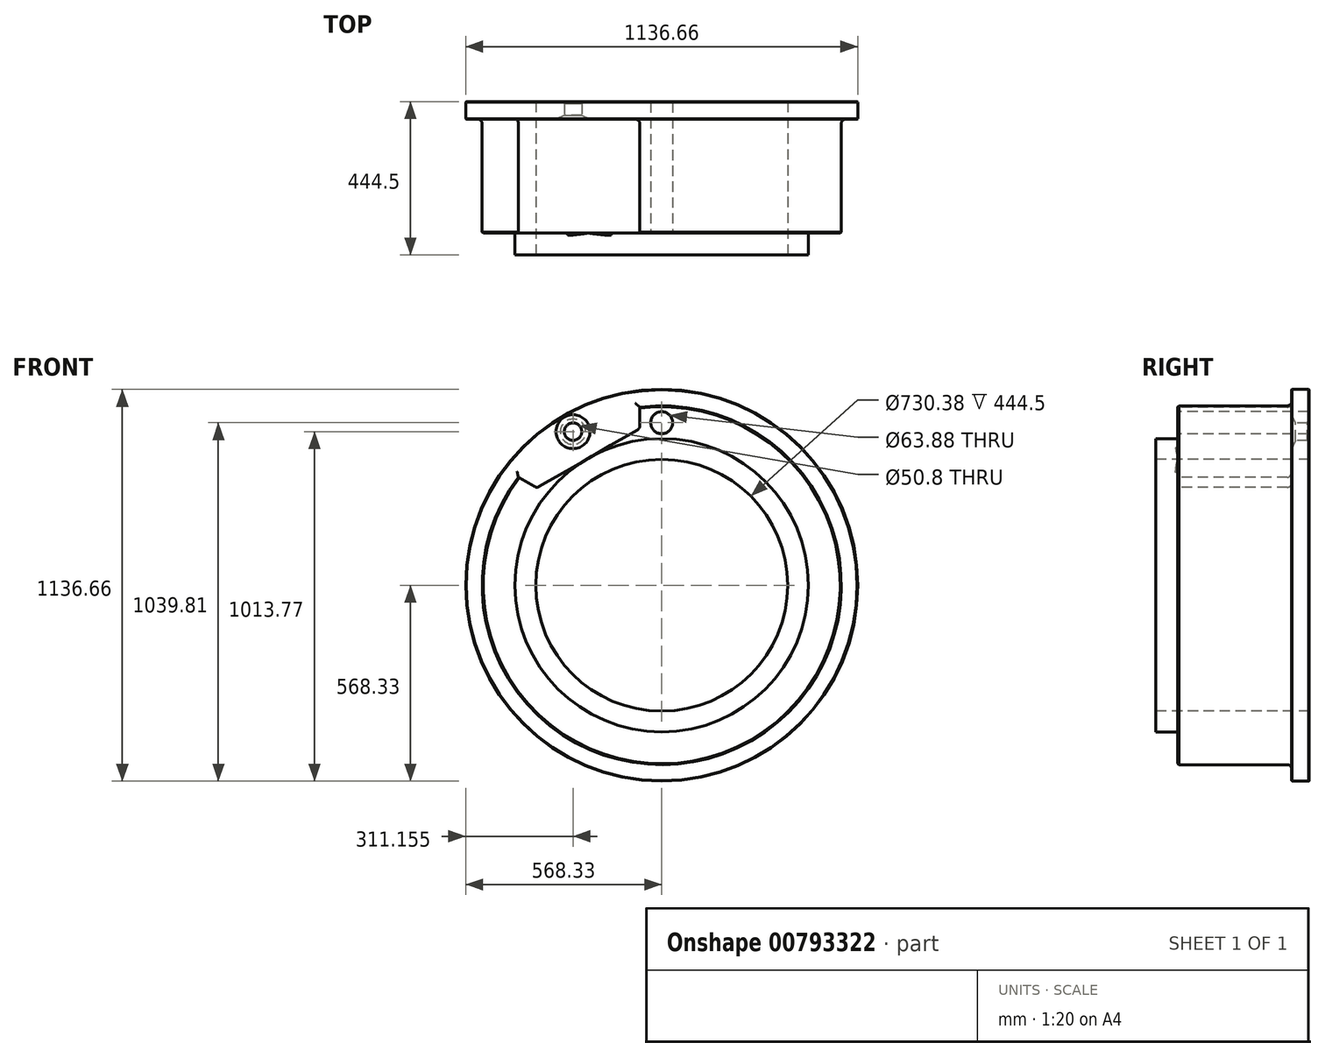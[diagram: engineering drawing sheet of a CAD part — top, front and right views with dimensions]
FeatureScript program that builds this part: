
annotation { "Feature Type Name" : "Feature", "Feature Type Description" : "" }
export const myFeature = defineFeature(function(context is Context, id is Id, definition is map)
    precondition{}
    {
        {
            var Q0;
            Q0=qCreatedBy(makeId("Front.planeOp"),FACE);
            var sketch = newSketch(context, id + "F0", { "sketchPlane" : qUnion([Q0])});
            skCircle(sketch, "E0", {"center": v(0, 0) * mm, "radius": 568.33 * mm});
            skSolve(sketch);
        }
        {
            var Q0;
            Q0 = qSketchRegion(id + "F0", true);
            extrude(context, id + "F1", {"entities" : qUnion([Q0]), "oppositeDirection" : true, "depth" : 444.5 * mm, "offsetDistance" : 25.4 * mm});
        }
        {
            var Q0;
            Q0=qCreatedBy(makeId("Front.planeOp"),FACE);
            var sketch = newSketch(context, id + "F2", { "sketchPlane" : qUnion([Q0])});
            skCircle(sketch, "E1", {"center": v(0, 0) * mm, "radius": 520.7 * mm});
            skCircle(sketch, "E2", {"center": v(0, 0) * mm, "radius": 587 * mm});
            skSolve(sketch);
        }
        {
            var Q0;
            Q0 = qSketchRegion(id + "F2", true);
            extrude(context, id + "F3", {"entities" : qUnion([Q0]), "operationType" : NewBodyOperationType.REMOVE, "oppositeDirection" : true, "depth" : 393.7 * mm, "offsetDistance" : 25.4 * mm});
        }
        {
            var Q0;
            Q0=qCreatedBy(makeId("Front.planeOp"),FACE);
            var sketch = newSketch(context, id + "F4", { "sketchPlane" : qUnion([Q0])});
            skCircle(sketch, "E3", {"center": v(0, 0) * mm, "radius": 425.45 * mm});
            skCircle(sketch, "E4", {"center": v(0, 0) * mm, "radius": 543.88 * mm});
            skSolve(sketch);
        }
        {
            var Q0;
            Q0 = qSketchRegion(id + "F4", true);
            extrude(context, id + "F5", {"entities" : qUnion([Q0]), "operationType" : NewBodyOperationType.REMOVE, "oppositeDirection" : true, "depth" : 63.5 * mm, "offsetDistance" : 25.4 * mm});
        }
        {
            var Q0;
            Q0=qCreatedBy(makeId("Front.planeOp"),FACE);
            var sketch = newSketch(context, id + "F6", { "sketchPlane" : qUnion([Q0])});
            skLineSegment(sketch, "E5", {"start": v(-63.5, 533.78) * mm, "end": v(-63.5, 454.6) * mm});
            skLineSegment(sketch, "E6", {"start": v(-430.52, 321.88) * mm, "end": v(-361.95, 282.3) * mm});
            skLineSegment(sketch, "E7", {"start": v(-63.5, 454.6) * mm, "end": v(-361.95, 282.3) * mm});
            skArc(sketch, "E8", {"start": v(-63.5, 533.78) * mm, "mid": v(-268.77, 465.53) * mm, "end": v(-430.52, 321.88) * mm});
            skSolve(sketch);
        }
        {
            var Q0;
            Q0 = qSketchRegion(id + "F6", true);
            extrude(context, id + "F7", {"entities" : qUnion([Q0]), "operationType" : NewBodyOperationType.REMOVE, "oppositeDirection" : true, "depth" : 393.7 * mm, "offsetDistance" : 25.4 * mm});
        }
        {
            var Q0;
            Q0=qCreatedBy(makeId("Front.planeOp"),FACE);
            var sketch = newSketch(context, id + "F8", { "sketchPlane" : qUnion([Q0])});
            skCircle(sketch, "E9", {"center": v(0, 0) * mm, "radius": 365.19 * mm});
            skSolve(sketch);
        }
        {
            var Q0;
            Q0 = qSketchRegion(id + "F8", true);
            extrude(context, id + "F9", {"entities" : qUnion([Q0]), "operationType" : NewBodyOperationType.REMOVE, "oppositeDirection" : true, "depth" : 447.04 * mm, "offsetDistance" : 25.4 * mm});
        }
        {
            var Q0;
            {var subQ0=sQuery(id+"F4.wireOp",EDGE,"E3");var subQ2=makeQuery(id+"F5.boolean.opBoolean","COPY",FACE,{"derivedFrom":makeQuery(id+"F5.opExtrude","CAP_FACE",FACE,{"disambiguationData":[OSD([subQ0,sQuery(id+"F4.wireOp",EDGE,"E4")])],"isStart":false})});Q0=makeQuery(id+"FbK9JrwXL36KEKy_1.1.F7.boolean.opBoolean","SPLIT",FACE,{"disambiguationData":[TD([makeQuery(id+"F7.boolean.opBoolean","COPY",FACE,{"derivedFrom":makeQuery(id+"F7.opExtrude","SWEPT_FACE",FACE,{"disambiguationData":[OSD([sQuery(id+"F6.wireOp",EDGE,"E6")])]})})])],"derivedFrom":subQ2});}
            var sketch = newSketch(context, id + "F10", { "sketchPlane" : qUnion([Q0])});
            skCircle(sketch, "E10", {"center": v(0, 471.47) * mm, "radius": 31.94 * mm});
            skSolve(sketch);
        }
        {
            var Q0;
            Q0 = qSketchRegion(id + "F10", true);
            extrude(context, id + "F11", {"entities" : qUnion([Q0]), "operationType" : NewBodyOperationType.REMOVE, "oppositeDirection" : true, "depth" : 447.04 * mm, "offsetDistance" : 25.4 * mm});
        }
        {
            var Q0;
            Q0=makeQuery(id+"F11.boolean.opBoolean","COPY",EDGE,{"derivedFrom":makeQuery(id+"F11.opExtrude","CAP_EDGE",EDGE,{"disambiguationData":[OSD([sQuery(id+"F10.wireOp",EDGE,"E10")])],"isStart":true})});
            var Q1;
            Q1=makeQuery(id+"FKzMlxL366D46Dd_1.1.F11.boolean.opBoolean","COPY",EDGE,{"derivedFrom":makeQuery(id+"FKzMlxL366D46Dd_1.1.F11.opExtrude","CAP_EDGE",EDGE,{"disambiguationData":[OSD([sQuery(id+"F10.wireOp",EDGE,"E10")])],"isStart":true})});
            var Q2;
            Q2=makeQuery(id+"FKzMlxL366D46Dd_1.2.F11.boolean.opBoolean","COPY",EDGE,{"derivedFrom":makeQuery(id+"FKzMlxL366D46Dd_1.2.F11.opExtrude","CAP_EDGE",EDGE,{"disambiguationData":[OSD([sQuery(id+"F10.wireOp",EDGE,"E10")])],"isStart":true})});
            var Q3;
            Q3=makeQuery(id+"FKzMlxL366D46Dd_1.3.F11.boolean.opBoolean","COPY",EDGE,{"derivedFrom":makeQuery(id+"FKzMlxL366D46Dd_1.3.F11.opExtrude","CAP_EDGE",EDGE,{"disambiguationData":[OSD([sQuery(id+"F10.wireOp",EDGE,"E10")])],"isStart":true})});
            var Q4;
            Q4=makeQuery(id+"FKzMlxL366D46Dd_1.4.F11.boolean.opBoolean","COPY",EDGE,{"derivedFrom":makeQuery(id+"FKzMlxL366D46Dd_1.4.F11.opExtrude","CAP_EDGE",EDGE,{"disambiguationData":[OSD([sQuery(id+"F10.wireOp",EDGE,"E10")])],"isStart":true})});
            var Q5;
            Q5=makeQuery(id+"FKzMlxL366D46Dd_1.5.F11.boolean.opBoolean","COPY",EDGE,{"derivedFrom":makeQuery(id+"FKzMlxL366D46Dd_1.5.F11.opExtrude","CAP_EDGE",EDGE,{"disambiguationData":[OSD([sQuery(id+"F10.wireOp",EDGE,"E10")])],"isStart":true})});
            var Q6;
            Q6=makeQuery(id+"FKzMlxL366D46Dd_1.5.F11.boolean.opBoolean","INTERSECT",EDGE,{"derivedFrom":[makeQuery(id+"F1.opExtrude","CAP_FACE",FACE,{"disambiguationData":[OSD([sQuery(id+"F0.wireOp",EDGE,"E0")])],"isStart":false}),makeQuery(id+"FKzMlxL366D46Dd_1.5.F11.opExtrude","SWEPT_FACE",FACE,{"disambiguationData":[OSD([sQuery(id+"F10.wireOp",EDGE,"E10")])]})]});
            var Q7;
            Q7=makeQuery(id+"FKzMlxL366D46Dd_1.4.F11.boolean.opBoolean","INTERSECT",EDGE,{"derivedFrom":[makeQuery(id+"F1.opExtrude","CAP_FACE",FACE,{"disambiguationData":[OSD([sQuery(id+"F0.wireOp",EDGE,"E0")])],"isStart":false}),makeQuery(id+"FKzMlxL366D46Dd_1.4.F11.opExtrude","SWEPT_FACE",FACE,{"disambiguationData":[OSD([sQuery(id+"F10.wireOp",EDGE,"E10")])]})]});
            var Q8;
            Q8=makeQuery(id+"F11.boolean.opBoolean","INTERSECT",EDGE,{"derivedFrom":[makeQuery(id+"F1.opExtrude","CAP_FACE",FACE,{"disambiguationData":[OSD([sQuery(id+"F0.wireOp",EDGE,"E0")])],"isStart":false}),makeQuery(id+"F11.opExtrude","SWEPT_FACE",FACE,{"disambiguationData":[OSD([sQuery(id+"F10.wireOp",EDGE,"E10")])]})]});
            var Q9;
            Q9=makeQuery(id+"FKzMlxL366D46Dd_1.3.F11.boolean.opBoolean","INTERSECT",EDGE,{"derivedFrom":[makeQuery(id+"F1.opExtrude","CAP_FACE",FACE,{"disambiguationData":[OSD([sQuery(id+"F0.wireOp",EDGE,"E0")])],"isStart":false}),makeQuery(id+"FKzMlxL366D46Dd_1.3.F11.opExtrude","SWEPT_FACE",FACE,{"disambiguationData":[OSD([sQuery(id+"F10.wireOp",EDGE,"E10")])]})]});
            var Q10;
            Q10=makeQuery(id+"FKzMlxL366D46Dd_1.1.F11.boolean.opBoolean","INTERSECT",EDGE,{"derivedFrom":[makeQuery(id+"F1.opExtrude","CAP_FACE",FACE,{"disambiguationData":[OSD([sQuery(id+"F0.wireOp",EDGE,"E0")])],"isStart":false}),makeQuery(id+"FKzMlxL366D46Dd_1.1.F11.opExtrude","SWEPT_FACE",FACE,{"disambiguationData":[OSD([sQuery(id+"F10.wireOp",EDGE,"E10")])]})]});
            var Q11;
            Q11=makeQuery(id+"FKzMlxL366D46Dd_1.2.F11.boolean.opBoolean","INTERSECT",EDGE,{"derivedFrom":[makeQuery(id+"F1.opExtrude","CAP_FACE",FACE,{"disambiguationData":[OSD([sQuery(id+"F0.wireOp",EDGE,"E0")])],"isStart":false}),makeQuery(id+"FKzMlxL366D46Dd_1.2.F11.opExtrude","SWEPT_FACE",FACE,{"disambiguationData":[OSD([sQuery(id+"F10.wireOp",EDGE,"E10")])]})]});
            var Q12;
            Q12=makeQuery(id+"F1.opExtrude","CAP_EDGE",EDGE,{"disambiguationData":[OSD([sQuery(id+"F0.wireOp",EDGE,"E0")])],"isStart":false});
            var Q13;
            Q13=makeQuery(id+"F3.boolean.opBoolean","INTERSECT",EDGE,{"derivedFrom":[makeQuery(id+"F1.opExtrude","SWEPT_FACE",FACE,{"disambiguationData":[OSD([sQuery(id+"F0.wireOp",EDGE,"E0")])]}),makeQuery(id+"F3.opExtrude","CAP_FACE",FACE,{"disambiguationData":[OSD([sQuery(id+"F2.wireOp",EDGE,"E1"),sQuery(id+"F2.wireOp",EDGE,"E2")])],"isStart":false})]});
            chamfer(context, id + "F12", {"entities" : qUnion([Q0, Q1, Q2, Q3, Q4, Q5, Q6, Q7, Q8, Q9, Q10, Q11, Q12, Q13]), "width" : 1.52 * mm, "tangentPropagation" : true});
        }
        {
            var Q0;
            {var subQ0=makeQuery(id+"F3.boolean.opBoolean","COPY",FACE,{"derivedFrom":makeQuery(id+"F3.opExtrude","SWEPT_FACE",FACE,{"disambiguationData":[OSD([sQuery(id+"F2.wireOp",EDGE,"E1")])]})});var subQ1=makeQuery(id+"F5.opExtrude","CAP_FACE",FACE,{"disambiguationData":[OSD([sQuery(id+"F4.wireOp",EDGE,"E3"),sQuery(id+"F4.wireOp",EDGE,"E4")])],"isStart":false});Q0=makeQuery(id+"FbK9JrwXL36KEKy_1.1.F7.boolean.opBoolean","SPLIT",EDGE,{"disambiguationData":[TD([makeQuery(id+"F7.boolean.opBoolean","COPY",FACE,{"derivedFrom":makeQuery(id+"F7.opExtrude","SWEPT_FACE",FACE,{"disambiguationData":[OSD([sQuery(id+"F6.wireOp",EDGE,"E6")])]})})])],"derivedFrom":makeQuery(id+"F5.boolean.opBoolean","INTERSECT",EDGE,{"derivedFrom":[subQ0,subQ1]})});}
            var Q1;
            {var subQ0=makeQuery(id+"F3.boolean.opBoolean","COPY",FACE,{"derivedFrom":makeQuery(id+"F3.opExtrude","SWEPT_FACE",FACE,{"disambiguationData":[OSD([sQuery(id+"F2.wireOp",EDGE,"E1")])]})});var subQ1=makeQuery(id+"F5.opExtrude","CAP_FACE",FACE,{"disambiguationData":[OSD([sQuery(id+"F4.wireOp",EDGE,"E3"),sQuery(id+"F4.wireOp",EDGE,"E4")])],"isStart":false});var subQ4=makeQuery(id+"F7.boolean.opBoolean","COPY",FACE,{"derivedFrom":makeQuery(id+"F7.opExtrude","SWEPT_FACE",FACE,{"disambiguationData":[OSD([sQuery(id+"F6.wireOp",EDGE,"E5")])]})});Q1=makeQuery(id+"FbK9JrwXL36KEKy_1.5.F7.boolean.opBoolean","SPLIT",EDGE,{"disambiguationData":[TD([subQ4])],"derivedFrom":makeQuery(id+"FbK9JrwXL36KEKy_1.4.F7.boolean.opBoolean","SPLIT",EDGE,{"disambiguationData":[TD([subQ4])],"derivedFrom":makeQuery(id+"FbK9JrwXL36KEKy_1.3.F7.boolean.opBoolean","SPLIT",EDGE,{"disambiguationData":[TD([subQ4])],"derivedFrom":makeQuery(id+"FbK9JrwXL36KEKy_1.2.F7.boolean.opBoolean","SPLIT",EDGE,{"disambiguationData":[TD([subQ4])],"derivedFrom":makeQuery(id+"FbK9JrwXL36KEKy_1.1.F7.boolean.opBoolean","SPLIT",EDGE,{"disambiguationData":[TD([subQ4])],"derivedFrom":makeQuery(id+"F5.boolean.opBoolean","INTERSECT",EDGE,{"derivedFrom":[subQ0,subQ1]})})})})})});}
            var Q2;
            Q2=makeQuery(id+"F5.boolean.opBoolean","COPY",EDGE,{"derivedFrom":makeQuery(id+"F5.opExtrude","CAP_EDGE",EDGE,{"disambiguationData":[OSD([sQuery(id+"F4.wireOp",EDGE,"E3")])],"isStart":true})});
            var Q3;
            {var subQ0=makeQuery(id+"F3.boolean.opBoolean","COPY",FACE,{"derivedFrom":makeQuery(id+"F3.opExtrude","SWEPT_FACE",FACE,{"disambiguationData":[OSD([sQuery(id+"F2.wireOp",EDGE,"E1")])]})});var subQ1=makeQuery(id+"F5.opExtrude","CAP_FACE",FACE,{"disambiguationData":[OSD([sQuery(id+"F4.wireOp",EDGE,"E3"),sQuery(id+"F4.wireOp",EDGE,"E4")])],"isStart":false});var subQ3=makeQuery(id+"FbK9JrwXL36KEKy_1.1.F7.opExtrude","SWEPT_FACE",FACE,{"disambiguationData":[OSD([sQuery(id+"F6.wireOp",EDGE,"E6")])]});var subQ4=sQuery(id+"F6.wireOp",EDGE,"E5");Q3=makeQuery(id+"FbK9JrwXL36KEKy_1.2.F7.boolean.opBoolean","SPLIT",EDGE,{"disambiguationData":[TD([makeQuery(id+"FbK9JrwXL36KEKy_1.1.F7.boolean.opBoolean","COPY",FACE,{"derivedFrom":subQ3})])],"derivedFrom":makeQuery(id+"FbK9JrwXL36KEKy_1.1.F7.boolean.opBoolean","SPLIT",EDGE,{"disambiguationData":[TD([makeQuery(id+"F7.boolean.opBoolean","COPY",FACE,{"derivedFrom":makeQuery(id+"F7.opExtrude","SWEPT_FACE",FACE,{"disambiguationData":[OSD([subQ4])]})})])],"derivedFrom":makeQuery(id+"F5.boolean.opBoolean","INTERSECT",EDGE,{"derivedFrom":[subQ0,subQ1]})})});}
            var Q4;
            {var subQ0=makeQuery(id+"F3.boolean.opBoolean","COPY",FACE,{"derivedFrom":makeQuery(id+"F3.opExtrude","SWEPT_FACE",FACE,{"disambiguationData":[OSD([sQuery(id+"F2.wireOp",EDGE,"E1")])]})});var subQ1=makeQuery(id+"F5.opExtrude","CAP_FACE",FACE,{"disambiguationData":[OSD([sQuery(id+"F4.wireOp",EDGE,"E3"),sQuery(id+"F4.wireOp",EDGE,"E4")])],"isStart":false});var subQ3=sQuery(id+"F6.wireOp",EDGE,"E5");var subQ4=sQuery(id+"F6.wireOp",EDGE,"E6");var subQ5=makeQuery(id+"FbK9JrwXL36KEKy_1.2.F7.opExtrude","SWEPT_FACE",FACE,{"disambiguationData":[OSD([subQ4])]});var subQ6=makeQuery(id+"F7.boolean.opBoolean","COPY",FACE,{"derivedFrom":makeQuery(id+"F7.opExtrude","SWEPT_FACE",FACE,{"disambiguationData":[OSD([subQ3])]})});Q4=makeQuery(id+"FbK9JrwXL36KEKy_1.3.F7.boolean.opBoolean","SPLIT",EDGE,{"disambiguationData":[TD([makeQuery(id+"FbK9JrwXL36KEKy_1.2.F7.boolean.opBoolean","COPY",FACE,{"derivedFrom":subQ5})])],"derivedFrom":makeQuery(id+"FbK9JrwXL36KEKy_1.2.F7.boolean.opBoolean","SPLIT",EDGE,{"disambiguationData":[TD([subQ6])],"derivedFrom":makeQuery(id+"FbK9JrwXL36KEKy_1.1.F7.boolean.opBoolean","SPLIT",EDGE,{"disambiguationData":[TD([subQ6])],"derivedFrom":makeQuery(id+"F5.boolean.opBoolean","INTERSECT",EDGE,{"derivedFrom":[subQ0,subQ1]})})})});}
            var Q5;
            {var subQ0=makeQuery(id+"F3.boolean.opBoolean","COPY",FACE,{"derivedFrom":makeQuery(id+"F3.opExtrude","SWEPT_FACE",FACE,{"disambiguationData":[OSD([sQuery(id+"F2.wireOp",EDGE,"E1")])]})});var subQ1=makeQuery(id+"F5.opExtrude","CAP_FACE",FACE,{"disambiguationData":[OSD([sQuery(id+"F4.wireOp",EDGE,"E3"),sQuery(id+"F4.wireOp",EDGE,"E4")])],"isStart":false});var subQ3=sQuery(id+"F6.wireOp",EDGE,"E6");var subQ4=makeQuery(id+"FbK9JrwXL36KEKy_1.3.F7.opExtrude","SWEPT_FACE",FACE,{"disambiguationData":[OSD([subQ3])]});var subQ5=sQuery(id+"F6.wireOp",EDGE,"E5");var subQ6=makeQuery(id+"F7.boolean.opBoolean","COPY",FACE,{"derivedFrom":makeQuery(id+"F7.opExtrude","SWEPT_FACE",FACE,{"disambiguationData":[OSD([subQ5])]})});Q5=makeQuery(id+"FbK9JrwXL36KEKy_1.4.F7.boolean.opBoolean","SPLIT",EDGE,{"disambiguationData":[TD([makeQuery(id+"FbK9JrwXL36KEKy_1.3.F7.boolean.opBoolean","COPY",FACE,{"derivedFrom":subQ4})])],"derivedFrom":makeQuery(id+"FbK9JrwXL36KEKy_1.3.F7.boolean.opBoolean","SPLIT",EDGE,{"disambiguationData":[TD([subQ6])],"derivedFrom":makeQuery(id+"FbK9JrwXL36KEKy_1.2.F7.boolean.opBoolean","SPLIT",EDGE,{"disambiguationData":[TD([subQ6])],"derivedFrom":makeQuery(id+"FbK9JrwXL36KEKy_1.1.F7.boolean.opBoolean","SPLIT",EDGE,{"disambiguationData":[TD([subQ6])],"derivedFrom":makeQuery(id+"F5.boolean.opBoolean","INTERSECT",EDGE,{"derivedFrom":[subQ0,subQ1]})})})})});}
            var Q6;
            {var subQ0=makeQuery(id+"F3.boolean.opBoolean","COPY",FACE,{"derivedFrom":makeQuery(id+"F3.opExtrude","SWEPT_FACE",FACE,{"disambiguationData":[OSD([sQuery(id+"F2.wireOp",EDGE,"E1")])]})});var subQ1=makeQuery(id+"F5.opExtrude","CAP_FACE",FACE,{"disambiguationData":[OSD([sQuery(id+"F4.wireOp",EDGE,"E3"),sQuery(id+"F4.wireOp",EDGE,"E4")])],"isStart":false});var subQ3=sQuery(id+"F6.wireOp",EDGE,"E6");var subQ4=makeQuery(id+"FbK9JrwXL36KEKy_1.4.F7.opExtrude","SWEPT_FACE",FACE,{"disambiguationData":[OSD([subQ3])]});var subQ5=sQuery(id+"F6.wireOp",EDGE,"E5");var subQ6=makeQuery(id+"F7.boolean.opBoolean","COPY",FACE,{"derivedFrom":makeQuery(id+"F7.opExtrude","SWEPT_FACE",FACE,{"disambiguationData":[OSD([subQ5])]})});Q6=makeQuery(id+"FbK9JrwXL36KEKy_1.5.F7.boolean.opBoolean","SPLIT",EDGE,{"disambiguationData":[TD([makeQuery(id+"FbK9JrwXL36KEKy_1.4.F7.boolean.opBoolean","COPY",FACE,{"derivedFrom":subQ4})])],"derivedFrom":makeQuery(id+"FbK9JrwXL36KEKy_1.4.F7.boolean.opBoolean","SPLIT",EDGE,{"disambiguationData":[TD([subQ6])],"derivedFrom":makeQuery(id+"FbK9JrwXL36KEKy_1.3.F7.boolean.opBoolean","SPLIT",EDGE,{"disambiguationData":[TD([subQ6])],"derivedFrom":makeQuery(id+"FbK9JrwXL36KEKy_1.2.F7.boolean.opBoolean","SPLIT",EDGE,{"disambiguationData":[TD([subQ6])],"derivedFrom":makeQuery(id+"FbK9JrwXL36KEKy_1.1.F7.boolean.opBoolean","SPLIT",EDGE,{"disambiguationData":[TD([subQ6])],"derivedFrom":makeQuery(id+"F5.boolean.opBoolean","INTERSECT",EDGE,{"derivedFrom":[subQ0,subQ1]})})})})})});}
            chamfer(context, id + "F13", {"entities" : qUnion([Q0, Q1, Q2, Q3, Q4, Q5, Q6]), "width" : 3.05 * mm, "tangentPropagation" : true});
        }
        {
            var Q0;
            {var subQ0=sQuery(id+"F4.wireOp",EDGE,"E3");var subQ2=sQuery(id+"F6.wireOp",EDGE,"E7");var subQ4=makeQuery(id+"FbK9JrwXL36KEKy_1.2.F7.opExtrude","SWEPT_FACE",FACE,{"disambiguationData":[OSD([subQ2])]});Q0=makeQuery(id+"FbK9JrwXL36KEKy_1.3.F7.boolean.opBoolean","SPLIT",EDGE,{"disambiguationData":[TD([makeQuery(id+"FbK9JrwXL36KEKy_1.2.F7.boolean.opBoolean","COPY",FACE,{"derivedFrom":subQ4})])],"derivedFrom":makeQuery(id+"FbK9JrwXL36KEKy_1.2.F7.boolean.opBoolean","SPLIT",EDGE,{"disambiguationData":[TD([makeQuery(id+"F7.boolean.opBoolean","COPY",FACE,{"derivedFrom":makeQuery(id+"F7.opExtrude","SWEPT_FACE",FACE,{"disambiguationData":[OSD([subQ2])]})})])],"derivedFrom":makeQuery(id+"FbK9JrwXL36KEKy_1.1.F7.boolean.opBoolean","SPLIT",EDGE,{"disambiguationData":[OD(0.0)],"derivedFrom":makeQuery(id+"F5.boolean.opBoolean","COPY",EDGE,{"derivedFrom":makeQuery(id+"F5.opExtrude","CAP_EDGE",EDGE,{"disambiguationData":[OSD([subQ0])],"isStart":false})})})})});}
            fillet(context, id + "F14", {"entities" : qUnion([Q0]), "radius" : 6.35 * mm, "tangentPropagation" : true, "allowEdgeOverflow" : false});
        }
        {
            var Q0;
            Q0=makeQuery(id+"FbK9JrwXL36KEKy_1.2.F7.boolean.opBoolean","COPY",EDGE,{"derivedFrom":makeQuery(id+"FbK9JrwXL36KEKy_1.2.F7.opExtrude","SWEPT_EDGE",EDGE,{"disambiguationData":[OSD([sQuery(id+"F6.wireOp",EDGE,"E5"),sQuery(id+"F6.wireOp",EDGE,"E7")])]})});
            var Q1;
            Q1=makeQuery(id+"FbK9JrwXL36KEKy_1.2.F7.boolean.opBoolean","COPY",EDGE,{"derivedFrom":makeQuery(id+"FbK9JrwXL36KEKy_1.2.F7.opExtrude","CAP_EDGE",EDGE,{"disambiguationData":[OSD([sQuery(id+"F6.wireOp",EDGE,"E7")])],"isStart":false})});
            var Q2;
            Q2=makeQuery(id+"FbK9JrwXL36KEKy_1.2.F7.boolean.opBoolean","COPY",EDGE,{"derivedFrom":makeQuery(id+"FbK9JrwXL36KEKy_1.2.F7.opExtrude","SWEPT_EDGE",EDGE,{"disambiguationData":[OSD([sQuery(id+"F6.wireOp",EDGE,"E6"),sQuery(id+"F6.wireOp",EDGE,"E7")])]})});
            var Q3;
            Q3=makeQuery(id+"FbK9JrwXL36KEKy_1.2.F7.boolean.opBoolean","COPY",EDGE,{"derivedFrom":makeQuery(id+"FbK9JrwXL36KEKy_1.2.F7.opExtrude","CAP_EDGE",EDGE,{"disambiguationData":[OSD([sQuery(id+"F6.wireOp",EDGE,"E5")])],"isStart":false})});
            var Q4;
            {var subQ2=sQuery(id+"F6.wireOp",EDGE,"E6");var subQ3=sQuery(id+"F6.wireOp",EDGE,"E5");var subQ5=sQuery(id+"F2.wireOp",EDGE,"E1");var subQ9=makeQuery(id+"FbK9JrwXL36KEKy_1.1.F7.opExtrude","SWEPT_FACE",FACE,{"disambiguationData":[OSD([subQ2])]});Q4=makeQuery(id+"FbK9JrwXL36KEKy_1.2.F7.boolean.opBoolean","SPLIT",EDGE,{"disambiguationData":[TD([makeQuery(id+"FbK9JrwXL36KEKy_1.1.F7.boolean.opBoolean","COPY",FACE,{"derivedFrom":subQ9})])],"derivedFrom":makeQuery(id+"FbK9JrwXL36KEKy_1.1.F7.boolean.opBoolean","SPLIT",EDGE,{"disambiguationData":[TD([makeQuery(id+"F7.boolean.opBoolean","COPY",FACE,{"derivedFrom":makeQuery(id+"F7.opExtrude","SWEPT_FACE",FACE,{"disambiguationData":[OSD([subQ3])]})})])],"derivedFrom":makeQuery(id+"F3.boolean.opBoolean","COPY",EDGE,{"derivedFrom":makeQuery(id+"F3.opExtrude","CAP_EDGE",EDGE,{"disambiguationData":[OSD([subQ5])],"isStart":false})})})});}
            var Q5;
            Q5=makeQuery(id+"FbK9JrwXL36KEKy_1.1.F7.boolean.opBoolean","COPY",EDGE,{"derivedFrom":makeQuery(id+"FbK9JrwXL36KEKy_1.1.F7.opExtrude","CAP_EDGE",EDGE,{"disambiguationData":[OSD([sQuery(id+"F6.wireOp",EDGE,"E7")])],"isStart":false})});
            var Q6;
            Q6=makeQuery(id+"FbK9JrwXL36KEKy_1.1.F7.boolean.opBoolean","COPY",EDGE,{"derivedFrom":makeQuery(id+"FbK9JrwXL36KEKy_1.1.F7.opExtrude","SWEPT_EDGE",EDGE,{"disambiguationData":[OSD([sQuery(id+"F6.wireOp",EDGE,"E5"),sQuery(id+"F6.wireOp",EDGE,"E7")])]})});
            var Q7;
            Q7=makeQuery(id+"FbK9JrwXL36KEKy_1.1.F7.boolean.opBoolean","COPY",EDGE,{"derivedFrom":makeQuery(id+"FbK9JrwXL36KEKy_1.1.F7.opExtrude","CAP_EDGE",EDGE,{"disambiguationData":[OSD([sQuery(id+"F6.wireOp",EDGE,"E5")])],"isStart":false})});
            var Q8;
            {var subQ2=sQuery(id+"F6.wireOp",EDGE,"E6");var subQ4=sQuery(id+"F2.wireOp",EDGE,"E1");Q8=makeQuery(id+"FbK9JrwXL36KEKy_1.1.F7.boolean.opBoolean","SPLIT",EDGE,{"disambiguationData":[TD([makeQuery(id+"F7.boolean.opBoolean","COPY",FACE,{"derivedFrom":makeQuery(id+"F7.opExtrude","SWEPT_FACE",FACE,{"disambiguationData":[OSD([subQ2])]})})])],"derivedFrom":makeQuery(id+"F3.boolean.opBoolean","COPY",EDGE,{"derivedFrom":makeQuery(id+"F3.opExtrude","CAP_EDGE",EDGE,{"disambiguationData":[OSD([subQ4])],"isStart":false})})});}
            var Q9;
            Q9=makeQuery(id+"FbK9JrwXL36KEKy_1.1.F7.boolean.opBoolean","COPY",EDGE,{"derivedFrom":makeQuery(id+"FbK9JrwXL36KEKy_1.1.F7.opExtrude","SWEPT_EDGE",EDGE,{"disambiguationData":[OSD([sQuery(id+"F6.wireOp",EDGE,"E6"),sQuery(id+"F6.wireOp",EDGE,"E7")])]})});
            var Q10;
            Q10=makeQuery(id+"FbK9JrwXL36KEKy_1.1.F7.boolean.opBoolean","COPY",EDGE,{"derivedFrom":makeQuery(id+"FbK9JrwXL36KEKy_1.1.F7.opExtrude","CAP_EDGE",EDGE,{"disambiguationData":[OSD([sQuery(id+"F6.wireOp",EDGE,"E6")])],"isStart":false})});
            var Q11;
            Q11=makeQuery(id+"F7.boolean.opBoolean","COPY",EDGE,{"derivedFrom":makeQuery(id+"F7.opExtrude","CAP_EDGE",EDGE,{"disambiguationData":[OSD([sQuery(id+"F6.wireOp",EDGE,"E6")])],"isStart":false})});
            var Q12;
            Q12=makeQuery(id+"F7.boolean.opBoolean","COPY",EDGE,{"derivedFrom":makeQuery(id+"F7.opExtrude","CAP_EDGE",EDGE,{"disambiguationData":[OSD([sQuery(id+"F6.wireOp",EDGE,"E7")])],"isStart":false})});
            var Q13;
            Q13=makeQuery(id+"F7.boolean.opBoolean","COPY",EDGE,{"derivedFrom":makeQuery(id+"F7.opExtrude","SWEPT_EDGE",EDGE,{"disambiguationData":[OSD([sQuery(id+"F6.wireOp",EDGE,"E6"),sQuery(id+"F6.wireOp",EDGE,"E7")])]})});
            var Q14;
            Q14=makeQuery(id+"F7.boolean.opBoolean","COPY",EDGE,{"derivedFrom":makeQuery(id+"F7.opExtrude","CAP_EDGE",EDGE,{"disambiguationData":[OSD([sQuery(id+"F6.wireOp",EDGE,"E5")])],"isStart":false})});
            var Q15;
            Q15=makeQuery(id+"F7.boolean.opBoolean","COPY",EDGE,{"derivedFrom":makeQuery(id+"F7.opExtrude","SWEPT_EDGE",EDGE,{"disambiguationData":[OSD([sQuery(id+"F6.wireOp",EDGE,"E5"),sQuery(id+"F6.wireOp",EDGE,"E7")])]})});
            var Q16;
            {var subQ0=sQuery(id+"F6.wireOp",EDGE,"E5");var subQ1=makeQuery(id+"F7.boolean.opBoolean","COPY",FACE,{"derivedFrom":makeQuery(id+"F7.opExtrude","SWEPT_FACE",FACE,{"disambiguationData":[OSD([subQ0])]})});var subQ2=sQuery(id+"F2.wireOp",EDGE,"E1");Q16=makeQuery(id+"FbK9JrwXL36KEKy_1.5.F7.boolean.opBoolean","SPLIT",EDGE,{"disambiguationData":[TD([subQ1])],"derivedFrom":makeQuery(id+"FbK9JrwXL36KEKy_1.4.F7.boolean.opBoolean","SPLIT",EDGE,{"disambiguationData":[TD([subQ1])],"derivedFrom":makeQuery(id+"FbK9JrwXL36KEKy_1.3.F7.boolean.opBoolean","SPLIT",EDGE,{"disambiguationData":[TD([subQ1])],"derivedFrom":makeQuery(id+"FbK9JrwXL36KEKy_1.2.F7.boolean.opBoolean","SPLIT",EDGE,{"disambiguationData":[TD([subQ1])],"derivedFrom":makeQuery(id+"FbK9JrwXL36KEKy_1.1.F7.boolean.opBoolean","SPLIT",EDGE,{"disambiguationData":[TD([subQ1])],"derivedFrom":makeQuery(id+"F3.boolean.opBoolean","COPY",EDGE,{"derivedFrom":makeQuery(id+"F3.opExtrude","CAP_EDGE",EDGE,{"disambiguationData":[OSD([subQ2])],"isStart":false})})})})})})});}
            var Q17;
            Q17=makeQuery(id+"FbK9JrwXL36KEKy_1.5.F7.boolean.opBoolean","COPY",EDGE,{"derivedFrom":makeQuery(id+"FbK9JrwXL36KEKy_1.5.F7.opExtrude","CAP_EDGE",EDGE,{"disambiguationData":[OSD([sQuery(id+"F6.wireOp",EDGE,"E6")])],"isStart":false})});
            var Q18;
            Q18=makeQuery(id+"FbK9JrwXL36KEKy_1.5.F7.boolean.opBoolean","COPY",EDGE,{"derivedFrom":makeQuery(id+"FbK9JrwXL36KEKy_1.5.F7.opExtrude","CAP_EDGE",EDGE,{"disambiguationData":[OSD([sQuery(id+"F6.wireOp",EDGE,"E7")])],"isStart":false})});
            var Q19;
            Q19=makeQuery(id+"FbK9JrwXL36KEKy_1.5.F7.boolean.opBoolean","COPY",EDGE,{"derivedFrom":makeQuery(id+"FbK9JrwXL36KEKy_1.5.F7.opExtrude","SWEPT_EDGE",EDGE,{"disambiguationData":[OSD([sQuery(id+"F6.wireOp",EDGE,"E6"),sQuery(id+"F6.wireOp",EDGE,"E7")])]})});
            var Q20;
            {var subQ2=sQuery(id+"F6.wireOp",EDGE,"E6");var subQ3=sQuery(id+"F6.wireOp",EDGE,"E5");var subQ5=sQuery(id+"F2.wireOp",EDGE,"E1");var subQ12=makeQuery(id+"FbK9JrwXL36KEKy_1.4.F7.opExtrude","SWEPT_FACE",FACE,{"disambiguationData":[OSD([subQ2])]});var subQ13=makeQuery(id+"F7.boolean.opBoolean","COPY",FACE,{"derivedFrom":makeQuery(id+"F7.opExtrude","SWEPT_FACE",FACE,{"disambiguationData":[OSD([subQ3])]})});Q20=makeQuery(id+"FbK9JrwXL36KEKy_1.5.F7.boolean.opBoolean","SPLIT",EDGE,{"disambiguationData":[TD([makeQuery(id+"FbK9JrwXL36KEKy_1.4.F7.boolean.opBoolean","COPY",FACE,{"derivedFrom":subQ12})])],"derivedFrom":makeQuery(id+"FbK9JrwXL36KEKy_1.4.F7.boolean.opBoolean","SPLIT",EDGE,{"disambiguationData":[TD([subQ13])],"derivedFrom":makeQuery(id+"FbK9JrwXL36KEKy_1.3.F7.boolean.opBoolean","SPLIT",EDGE,{"disambiguationData":[TD([subQ13])],"derivedFrom":makeQuery(id+"FbK9JrwXL36KEKy_1.2.F7.boolean.opBoolean","SPLIT",EDGE,{"disambiguationData":[TD([subQ13])],"derivedFrom":makeQuery(id+"FbK9JrwXL36KEKy_1.1.F7.boolean.opBoolean","SPLIT",EDGE,{"disambiguationData":[TD([subQ13])],"derivedFrom":makeQuery(id+"F3.boolean.opBoolean","COPY",EDGE,{"derivedFrom":makeQuery(id+"F3.opExtrude","CAP_EDGE",EDGE,{"disambiguationData":[OSD([subQ5])],"isStart":false})})})})})})});}
            var Q21;
            Q21=makeQuery(id+"FbK9JrwXL36KEKy_1.5.F7.boolean.opBoolean","COPY",EDGE,{"derivedFrom":makeQuery(id+"FbK9JrwXL36KEKy_1.5.F7.opExtrude","SWEPT_EDGE",EDGE,{"disambiguationData":[OSD([sQuery(id+"F6.wireOp",EDGE,"E5"),sQuery(id+"F6.wireOp",EDGE,"E7")])]})});
            var Q22;
            Q22=makeQuery(id+"FbK9JrwXL36KEKy_1.5.F7.boolean.opBoolean","COPY",EDGE,{"derivedFrom":makeQuery(id+"FbK9JrwXL36KEKy_1.5.F7.opExtrude","CAP_EDGE",EDGE,{"disambiguationData":[OSD([sQuery(id+"F6.wireOp",EDGE,"E5")])],"isStart":false})});
            var Q23;
            Q23=makeQuery(id+"FbK9JrwXL36KEKy_1.4.F7.boolean.opBoolean","COPY",EDGE,{"derivedFrom":makeQuery(id+"FbK9JrwXL36KEKy_1.4.F7.opExtrude","CAP_EDGE",EDGE,{"disambiguationData":[OSD([sQuery(id+"F6.wireOp",EDGE,"E6")])],"isStart":false})});
            var Q24;
            Q24=makeQuery(id+"FbK9JrwXL36KEKy_1.4.F7.boolean.opBoolean","COPY",EDGE,{"derivedFrom":makeQuery(id+"FbK9JrwXL36KEKy_1.4.F7.opExtrude","SWEPT_EDGE",EDGE,{"disambiguationData":[OSD([sQuery(id+"F6.wireOp",EDGE,"E6"),sQuery(id+"F6.wireOp",EDGE,"E7")])]})});
            var Q25;
            Q25=makeQuery(id+"FbK9JrwXL36KEKy_1.4.F7.boolean.opBoolean","COPY",EDGE,{"derivedFrom":makeQuery(id+"FbK9JrwXL36KEKy_1.4.F7.opExtrude","CAP_EDGE",EDGE,{"disambiguationData":[OSD([sQuery(id+"F6.wireOp",EDGE,"E7")])],"isStart":false})});
            var Q26;
            Q26=makeQuery(id+"FbK9JrwXL36KEKy_1.4.F7.boolean.opBoolean","COPY",EDGE,{"derivedFrom":makeQuery(id+"FbK9JrwXL36KEKy_1.4.F7.opExtrude","SWEPT_EDGE",EDGE,{"disambiguationData":[OSD([sQuery(id+"F6.wireOp",EDGE,"E5"),sQuery(id+"F6.wireOp",EDGE,"E7")])]})});
            var Q27;
            Q27=makeQuery(id+"FbK9JrwXL36KEKy_1.4.F7.boolean.opBoolean","COPY",EDGE,{"derivedFrom":makeQuery(id+"FbK9JrwXL36KEKy_1.4.F7.opExtrude","CAP_EDGE",EDGE,{"disambiguationData":[OSD([sQuery(id+"F6.wireOp",EDGE,"E5")])],"isStart":false})});
            var Q28;
            {var subQ2=sQuery(id+"F6.wireOp",EDGE,"E6");var subQ3=sQuery(id+"F6.wireOp",EDGE,"E5");var subQ5=sQuery(id+"F2.wireOp",EDGE,"E1");var subQ11=makeQuery(id+"FbK9JrwXL36KEKy_1.3.F7.opExtrude","SWEPT_FACE",FACE,{"disambiguationData":[OSD([subQ2])]});var subQ12=makeQuery(id+"F7.boolean.opBoolean","COPY",FACE,{"derivedFrom":makeQuery(id+"F7.opExtrude","SWEPT_FACE",FACE,{"disambiguationData":[OSD([subQ3])]})});Q28=makeQuery(id+"FbK9JrwXL36KEKy_1.4.F7.boolean.opBoolean","SPLIT",EDGE,{"disambiguationData":[TD([makeQuery(id+"FbK9JrwXL36KEKy_1.3.F7.boolean.opBoolean","COPY",FACE,{"derivedFrom":subQ11})])],"derivedFrom":makeQuery(id+"FbK9JrwXL36KEKy_1.3.F7.boolean.opBoolean","SPLIT",EDGE,{"disambiguationData":[TD([subQ12])],"derivedFrom":makeQuery(id+"FbK9JrwXL36KEKy_1.2.F7.boolean.opBoolean","SPLIT",EDGE,{"disambiguationData":[TD([subQ12])],"derivedFrom":makeQuery(id+"FbK9JrwXL36KEKy_1.1.F7.boolean.opBoolean","SPLIT",EDGE,{"disambiguationData":[TD([subQ12])],"derivedFrom":makeQuery(id+"F3.boolean.opBoolean","COPY",EDGE,{"derivedFrom":makeQuery(id+"F3.opExtrude","CAP_EDGE",EDGE,{"disambiguationData":[OSD([subQ5])],"isStart":false})})})})})});}
            var Q29;
            Q29=makeQuery(id+"FbK9JrwXL36KEKy_1.3.F7.boolean.opBoolean","COPY",EDGE,{"derivedFrom":makeQuery(id+"FbK9JrwXL36KEKy_1.3.F7.opExtrude","SWEPT_EDGE",EDGE,{"disambiguationData":[OSD([sQuery(id+"F6.wireOp",EDGE,"E6"),sQuery(id+"F6.wireOp",EDGE,"E7")])]})});
            var Q30;
            Q30=makeQuery(id+"FbK9JrwXL36KEKy_1.3.F7.boolean.opBoolean","COPY",EDGE,{"derivedFrom":makeQuery(id+"FbK9JrwXL36KEKy_1.3.F7.opExtrude","CAP_EDGE",EDGE,{"disambiguationData":[OSD([sQuery(id+"F6.wireOp",EDGE,"E6")])],"isStart":false})});
            var Q31;
            Q31=makeQuery(id+"FbK9JrwXL36KEKy_1.3.F7.boolean.opBoolean","COPY",EDGE,{"derivedFrom":makeQuery(id+"FbK9JrwXL36KEKy_1.3.F7.opExtrude","CAP_EDGE",EDGE,{"disambiguationData":[OSD([sQuery(id+"F6.wireOp",EDGE,"E7")])],"isStart":false})});
            var Q32;
            Q32=makeQuery(id+"FbK9JrwXL36KEKy_1.3.F7.boolean.opBoolean","COPY",EDGE,{"derivedFrom":makeQuery(id+"FbK9JrwXL36KEKy_1.3.F7.opExtrude","SWEPT_EDGE",EDGE,{"disambiguationData":[OSD([sQuery(id+"F6.wireOp",EDGE,"E5"),sQuery(id+"F6.wireOp",EDGE,"E7")])]})});
            var Q33;
            Q33=makeQuery(id+"FbK9JrwXL36KEKy_1.3.F7.boolean.opBoolean","COPY",EDGE,{"derivedFrom":makeQuery(id+"FbK9JrwXL36KEKy_1.3.F7.opExtrude","CAP_EDGE",EDGE,{"disambiguationData":[OSD([sQuery(id+"F6.wireOp",EDGE,"E5")])],"isStart":false})});
            var Q34;
            {var subQ2=sQuery(id+"F6.wireOp",EDGE,"E6");var subQ3=sQuery(id+"F6.wireOp",EDGE,"E5");var subQ5=sQuery(id+"F2.wireOp",EDGE,"E1");var subQ10=makeQuery(id+"FbK9JrwXL36KEKy_1.2.F7.opExtrude","SWEPT_FACE",FACE,{"disambiguationData":[OSD([subQ2])]});var subQ11=makeQuery(id+"F7.boolean.opBoolean","COPY",FACE,{"derivedFrom":makeQuery(id+"F7.opExtrude","SWEPT_FACE",FACE,{"disambiguationData":[OSD([subQ3])]})});Q34=makeQuery(id+"FbK9JrwXL36KEKy_1.3.F7.boolean.opBoolean","SPLIT",EDGE,{"disambiguationData":[TD([makeQuery(id+"FbK9JrwXL36KEKy_1.2.F7.boolean.opBoolean","COPY",FACE,{"derivedFrom":subQ10})])],"derivedFrom":makeQuery(id+"FbK9JrwXL36KEKy_1.2.F7.boolean.opBoolean","SPLIT",EDGE,{"disambiguationData":[TD([subQ11])],"derivedFrom":makeQuery(id+"FbK9JrwXL36KEKy_1.1.F7.boolean.opBoolean","SPLIT",EDGE,{"disambiguationData":[TD([subQ11])],"derivedFrom":makeQuery(id+"F3.boolean.opBoolean","COPY",EDGE,{"derivedFrom":makeQuery(id+"F3.opExtrude","CAP_EDGE",EDGE,{"disambiguationData":[OSD([subQ5])],"isStart":false})})})})});}
            var Q35;
            Q35=makeQuery(id+"FbK9JrwXL36KEKy_1.2.F7.boolean.opBoolean","COPY",EDGE,{"derivedFrom":makeQuery(id+"FbK9JrwXL36KEKy_1.2.F7.opExtrude","CAP_EDGE",EDGE,{"disambiguationData":[OSD([sQuery(id+"F6.wireOp",EDGE,"E6")])],"isStart":false})});
            fillet(context, id + "F15", {"entities" : qUnion([Q0, Q1, Q2, Q3, Q4, Q5, Q6, Q7, Q8, Q9, Q10, Q11, Q12, Q13, Q14, Q15, Q16, Q17, Q18, Q19, Q20, Q21, Q22, Q23, Q24, Q25, Q26, Q27, Q28, Q29, Q30, Q31, Q32, Q33, Q34, Q35]), "radius" : 12.7 * mm, "tangentPropagation" : true, "allowEdgeOverflow" : false});
        }
        {
            var Q0;
            Q0=qCreatedBy(makeId("Front.planeOp"),FACE);
            var sketch = newSketch(context, id + "F16", { "sketchPlane" : qUnion([Q0])});
            skCircle(sketch, "E11", {"center": v(-257.18, 445.44) * mm, "radius": 25.4 * mm});
            skLineSegment(sketch, "E12", {"start": v(0, 0) * mm, "end": v(-257.18, 445.44) * mm, "construction": true});
            skSolve(sketch);
        }
        {
            var Q0;
            Q0 = qSketchRegion(id + "F16", true);
            extrude(context, id + "F17", {"entities" : qUnion([Q0]), "operationType" : NewBodyOperationType.REMOVE, "oppositeDirection" : true, "depth" : 447.04 * mm, "offsetDistance" : 25.4 * mm});
        }
        {
            var Q0;
            {var subQ0=sQuery(id+"F6.wireOp",EDGE,"E8");var subQ1=sQuery(id+"F6.wireOp",EDGE,"E7");var subQ2=sQuery(id+"F6.wireOp",EDGE,"E6");var subQ3=sQuery(id+"F6.wireOp",EDGE,"E5");Q0=makeQuery(id+"F17.boolean.opBoolean","INTERSECT",EDGE,{"derivedFrom":[makeQuery(id+"FbK9JrwXL36KEKy_1.5.F7.boolean.opBoolean","MERGE",FACE,{"derivedFrom":[makeQuery(id+"FbK9JrwXL36KEKy_1.4.F7.boolean.opBoolean","MERGE",FACE,{"derivedFrom":[makeQuery(id+"FbK9JrwXL36KEKy_1.3.F7.boolean.opBoolean","MERGE",FACE,{"derivedFrom":[makeQuery(id+"FbK9JrwXL36KEKy_1.2.F7.boolean.opBoolean","MERGE",FACE,{"derivedFrom":[makeQuery(id+"FbK9JrwXL36KEKy_1.1.F7.boolean.opBoolean","MERGE",FACE,{"derivedFrom":[makeQuery(id+"F7.boolean.opBoolean","MERGE",FACE,{"derivedFrom":[makeQuery(id+"F3.boolean.opBoolean","COPY",FACE,{"derivedFrom":makeQuery(id+"F3.opExtrude","CAP_FACE",FACE,{"disambiguationData":[OSD([sQuery(id+"F2.wireOp",EDGE,"E1"),sQuery(id+"F2.wireOp",EDGE,"E2")])],"isStart":false})}),makeQuery(id+"F7.opExtrude","CAP_FACE",FACE,{"disambiguationData":[OSD([subQ3,subQ2,subQ1,subQ0])],"isStart":false})]}),makeQuery(id+"FbK9JrwXL36KEKy_1.1.F7.opExtrude","CAP_FACE",FACE,{"disambiguationData":[OSD([subQ3,subQ2,subQ1,subQ0])],"isStart":false})]}),makeQuery(id+"FbK9JrwXL36KEKy_1.2.F7.opExtrude","CAP_FACE",FACE,{"disambiguationData":[OSD([subQ3,subQ2,subQ1,subQ0])],"isStart":false})]}),makeQuery(id+"FbK9JrwXL36KEKy_1.3.F7.opExtrude","CAP_FACE",FACE,{"disambiguationData":[OSD([subQ3,subQ2,subQ1,subQ0])],"isStart":false})]}),makeQuery(id+"FbK9JrwXL36KEKy_1.4.F7.opExtrude","CAP_FACE",FACE,{"disambiguationData":[OSD([subQ3,subQ2,subQ1,subQ0])],"isStart":false})]}),makeQuery(id+"FbK9JrwXL36KEKy_1.5.F7.opExtrude","CAP_FACE",FACE,{"disambiguationData":[OSD([subQ3,subQ2,subQ1,subQ0])],"isStart":false})]}),makeQuery(id+"F17.opExtrude","SWEPT_FACE",FACE,{"disambiguationData":[OSD([sQuery(id+"F16.wireOp",EDGE,"E11")])]})]});}
            var Q1;
            {var subQ0=sQuery(id+"F6.wireOp",EDGE,"E8");var subQ1=sQuery(id+"F6.wireOp",EDGE,"E7");var subQ2=sQuery(id+"F6.wireOp",EDGE,"E6");var subQ3=sQuery(id+"F6.wireOp",EDGE,"E5");Q1=makeQuery(id+"FozZmEnTaBS6IKp_1.1.F17.boolean.opBoolean","INTERSECT",EDGE,{"derivedFrom":[makeQuery(id+"FbK9JrwXL36KEKy_1.5.F7.boolean.opBoolean","MERGE",FACE,{"derivedFrom":[makeQuery(id+"FbK9JrwXL36KEKy_1.4.F7.boolean.opBoolean","MERGE",FACE,{"derivedFrom":[makeQuery(id+"FbK9JrwXL36KEKy_1.3.F7.boolean.opBoolean","MERGE",FACE,{"derivedFrom":[makeQuery(id+"FbK9JrwXL36KEKy_1.2.F7.boolean.opBoolean","MERGE",FACE,{"derivedFrom":[makeQuery(id+"FbK9JrwXL36KEKy_1.1.F7.boolean.opBoolean","MERGE",FACE,{"derivedFrom":[makeQuery(id+"F7.boolean.opBoolean","MERGE",FACE,{"derivedFrom":[makeQuery(id+"F3.boolean.opBoolean","COPY",FACE,{"derivedFrom":makeQuery(id+"F3.opExtrude","CAP_FACE",FACE,{"disambiguationData":[OSD([sQuery(id+"F2.wireOp",EDGE,"E1"),sQuery(id+"F2.wireOp",EDGE,"E2")])],"isStart":false})}),makeQuery(id+"F7.opExtrude","CAP_FACE",FACE,{"disambiguationData":[OSD([subQ3,subQ2,subQ1,subQ0])],"isStart":false})]}),makeQuery(id+"FbK9JrwXL36KEKy_1.1.F7.opExtrude","CAP_FACE",FACE,{"disambiguationData":[OSD([subQ3,subQ2,subQ1,subQ0])],"isStart":false})]}),makeQuery(id+"FbK9JrwXL36KEKy_1.2.F7.opExtrude","CAP_FACE",FACE,{"disambiguationData":[OSD([subQ3,subQ2,subQ1,subQ0])],"isStart":false})]}),makeQuery(id+"FbK9JrwXL36KEKy_1.3.F7.opExtrude","CAP_FACE",FACE,{"disambiguationData":[OSD([subQ3,subQ2,subQ1,subQ0])],"isStart":false})]}),makeQuery(id+"FbK9JrwXL36KEKy_1.4.F7.opExtrude","CAP_FACE",FACE,{"disambiguationData":[OSD([subQ3,subQ2,subQ1,subQ0])],"isStart":false})]}),makeQuery(id+"FbK9JrwXL36KEKy_1.5.F7.opExtrude","CAP_FACE",FACE,{"disambiguationData":[OSD([subQ3,subQ2,subQ1,subQ0])],"isStart":false})]}),makeQuery(id+"FozZmEnTaBS6IKp_1.1.F17.opExtrude","SWEPT_FACE",FACE,{"disambiguationData":[OSD([sQuery(id+"F16.wireOp",EDGE,"E11")])]})]});}
            var Q2;
            {var subQ0=sQuery(id+"F6.wireOp",EDGE,"E8");var subQ1=sQuery(id+"F6.wireOp",EDGE,"E7");var subQ2=sQuery(id+"F6.wireOp",EDGE,"E6");var subQ3=sQuery(id+"F6.wireOp",EDGE,"E5");Q2=makeQuery(id+"FozZmEnTaBS6IKp_1.2.F17.boolean.opBoolean","INTERSECT",EDGE,{"derivedFrom":[makeQuery(id+"FbK9JrwXL36KEKy_1.5.F7.boolean.opBoolean","MERGE",FACE,{"derivedFrom":[makeQuery(id+"FbK9JrwXL36KEKy_1.4.F7.boolean.opBoolean","MERGE",FACE,{"derivedFrom":[makeQuery(id+"FbK9JrwXL36KEKy_1.3.F7.boolean.opBoolean","MERGE",FACE,{"derivedFrom":[makeQuery(id+"FbK9JrwXL36KEKy_1.2.F7.boolean.opBoolean","MERGE",FACE,{"derivedFrom":[makeQuery(id+"FbK9JrwXL36KEKy_1.1.F7.boolean.opBoolean","MERGE",FACE,{"derivedFrom":[makeQuery(id+"F7.boolean.opBoolean","MERGE",FACE,{"derivedFrom":[makeQuery(id+"F3.boolean.opBoolean","COPY",FACE,{"derivedFrom":makeQuery(id+"F3.opExtrude","CAP_FACE",FACE,{"disambiguationData":[OSD([sQuery(id+"F2.wireOp",EDGE,"E1"),sQuery(id+"F2.wireOp",EDGE,"E2")])],"isStart":false})}),makeQuery(id+"F7.opExtrude","CAP_FACE",FACE,{"disambiguationData":[OSD([subQ3,subQ2,subQ1,subQ0])],"isStart":false})]}),makeQuery(id+"FbK9JrwXL36KEKy_1.1.F7.opExtrude","CAP_FACE",FACE,{"disambiguationData":[OSD([subQ3,subQ2,subQ1,subQ0])],"isStart":false})]}),makeQuery(id+"FbK9JrwXL36KEKy_1.2.F7.opExtrude","CAP_FACE",FACE,{"disambiguationData":[OSD([subQ3,subQ2,subQ1,subQ0])],"isStart":false})]}),makeQuery(id+"FbK9JrwXL36KEKy_1.3.F7.opExtrude","CAP_FACE",FACE,{"disambiguationData":[OSD([subQ3,subQ2,subQ1,subQ0])],"isStart":false})]}),makeQuery(id+"FbK9JrwXL36KEKy_1.4.F7.opExtrude","CAP_FACE",FACE,{"disambiguationData":[OSD([subQ3,subQ2,subQ1,subQ0])],"isStart":false})]}),makeQuery(id+"FbK9JrwXL36KEKy_1.5.F7.opExtrude","CAP_FACE",FACE,{"disambiguationData":[OSD([subQ3,subQ2,subQ1,subQ0])],"isStart":false})]}),makeQuery(id+"FozZmEnTaBS6IKp_1.2.F17.opExtrude","SWEPT_FACE",FACE,{"disambiguationData":[OSD([sQuery(id+"F16.wireOp",EDGE,"E11")])]})]});}
            var Q3;
            {var subQ0=sQuery(id+"F6.wireOp",EDGE,"E8");var subQ1=sQuery(id+"F6.wireOp",EDGE,"E7");var subQ2=sQuery(id+"F6.wireOp",EDGE,"E6");var subQ3=sQuery(id+"F6.wireOp",EDGE,"E5");Q3=makeQuery(id+"FozZmEnTaBS6IKp_1.5.F17.boolean.opBoolean","INTERSECT",EDGE,{"derivedFrom":[makeQuery(id+"FbK9JrwXL36KEKy_1.5.F7.boolean.opBoolean","MERGE",FACE,{"derivedFrom":[makeQuery(id+"FbK9JrwXL36KEKy_1.4.F7.boolean.opBoolean","MERGE",FACE,{"derivedFrom":[makeQuery(id+"FbK9JrwXL36KEKy_1.3.F7.boolean.opBoolean","MERGE",FACE,{"derivedFrom":[makeQuery(id+"FbK9JrwXL36KEKy_1.2.F7.boolean.opBoolean","MERGE",FACE,{"derivedFrom":[makeQuery(id+"FbK9JrwXL36KEKy_1.1.F7.boolean.opBoolean","MERGE",FACE,{"derivedFrom":[makeQuery(id+"F7.boolean.opBoolean","MERGE",FACE,{"derivedFrom":[makeQuery(id+"F3.boolean.opBoolean","COPY",FACE,{"derivedFrom":makeQuery(id+"F3.opExtrude","CAP_FACE",FACE,{"disambiguationData":[OSD([sQuery(id+"F2.wireOp",EDGE,"E1"),sQuery(id+"F2.wireOp",EDGE,"E2")])],"isStart":false})}),makeQuery(id+"F7.opExtrude","CAP_FACE",FACE,{"disambiguationData":[OSD([subQ3,subQ2,subQ1,subQ0])],"isStart":false})]}),makeQuery(id+"FbK9JrwXL36KEKy_1.1.F7.opExtrude","CAP_FACE",FACE,{"disambiguationData":[OSD([subQ3,subQ2,subQ1,subQ0])],"isStart":false})]}),makeQuery(id+"FbK9JrwXL36KEKy_1.2.F7.opExtrude","CAP_FACE",FACE,{"disambiguationData":[OSD([subQ3,subQ2,subQ1,subQ0])],"isStart":false})]}),makeQuery(id+"FbK9JrwXL36KEKy_1.3.F7.opExtrude","CAP_FACE",FACE,{"disambiguationData":[OSD([subQ3,subQ2,subQ1,subQ0])],"isStart":false})]}),makeQuery(id+"FbK9JrwXL36KEKy_1.4.F7.opExtrude","CAP_FACE",FACE,{"disambiguationData":[OSD([subQ3,subQ2,subQ1,subQ0])],"isStart":false})]}),makeQuery(id+"FbK9JrwXL36KEKy_1.5.F7.opExtrude","CAP_FACE",FACE,{"disambiguationData":[OSD([subQ3,subQ2,subQ1,subQ0])],"isStart":false})]}),makeQuery(id+"FozZmEnTaBS6IKp_1.5.F17.opExtrude","SWEPT_FACE",FACE,{"disambiguationData":[OSD([sQuery(id+"F16.wireOp",EDGE,"E11")])]})]});}
            var Q4;
            {var subQ0=sQuery(id+"F6.wireOp",EDGE,"E8");var subQ1=sQuery(id+"F6.wireOp",EDGE,"E7");var subQ2=sQuery(id+"F6.wireOp",EDGE,"E6");var subQ3=sQuery(id+"F6.wireOp",EDGE,"E5");Q4=makeQuery(id+"FozZmEnTaBS6IKp_1.4.F17.boolean.opBoolean","INTERSECT",EDGE,{"derivedFrom":[makeQuery(id+"FbK9JrwXL36KEKy_1.5.F7.boolean.opBoolean","MERGE",FACE,{"derivedFrom":[makeQuery(id+"FbK9JrwXL36KEKy_1.4.F7.boolean.opBoolean","MERGE",FACE,{"derivedFrom":[makeQuery(id+"FbK9JrwXL36KEKy_1.3.F7.boolean.opBoolean","MERGE",FACE,{"derivedFrom":[makeQuery(id+"FbK9JrwXL36KEKy_1.2.F7.boolean.opBoolean","MERGE",FACE,{"derivedFrom":[makeQuery(id+"FbK9JrwXL36KEKy_1.1.F7.boolean.opBoolean","MERGE",FACE,{"derivedFrom":[makeQuery(id+"F7.boolean.opBoolean","MERGE",FACE,{"derivedFrom":[makeQuery(id+"F3.boolean.opBoolean","COPY",FACE,{"derivedFrom":makeQuery(id+"F3.opExtrude","CAP_FACE",FACE,{"disambiguationData":[OSD([sQuery(id+"F2.wireOp",EDGE,"E1"),sQuery(id+"F2.wireOp",EDGE,"E2")])],"isStart":false})}),makeQuery(id+"F7.opExtrude","CAP_FACE",FACE,{"disambiguationData":[OSD([subQ3,subQ2,subQ1,subQ0])],"isStart":false})]}),makeQuery(id+"FbK9JrwXL36KEKy_1.1.F7.opExtrude","CAP_FACE",FACE,{"disambiguationData":[OSD([subQ3,subQ2,subQ1,subQ0])],"isStart":false})]}),makeQuery(id+"FbK9JrwXL36KEKy_1.2.F7.opExtrude","CAP_FACE",FACE,{"disambiguationData":[OSD([subQ3,subQ2,subQ1,subQ0])],"isStart":false})]}),makeQuery(id+"FbK9JrwXL36KEKy_1.3.F7.opExtrude","CAP_FACE",FACE,{"disambiguationData":[OSD([subQ3,subQ2,subQ1,subQ0])],"isStart":false})]}),makeQuery(id+"FbK9JrwXL36KEKy_1.4.F7.opExtrude","CAP_FACE",FACE,{"disambiguationData":[OSD([subQ3,subQ2,subQ1,subQ0])],"isStart":false})]}),makeQuery(id+"FbK9JrwXL36KEKy_1.5.F7.opExtrude","CAP_FACE",FACE,{"disambiguationData":[OSD([subQ3,subQ2,subQ1,subQ0])],"isStart":false})]}),makeQuery(id+"FozZmEnTaBS6IKp_1.4.F17.opExtrude","SWEPT_FACE",FACE,{"disambiguationData":[OSD([sQuery(id+"F16.wireOp",EDGE,"E11")])]})]});}
            var Q5;
            {var subQ0=sQuery(id+"F6.wireOp",EDGE,"E8");var subQ1=sQuery(id+"F6.wireOp",EDGE,"E7");var subQ2=sQuery(id+"F6.wireOp",EDGE,"E6");var subQ3=sQuery(id+"F6.wireOp",EDGE,"E5");Q5=makeQuery(id+"FozZmEnTaBS6IKp_1.3.F17.boolean.opBoolean","INTERSECT",EDGE,{"derivedFrom":[makeQuery(id+"FbK9JrwXL36KEKy_1.5.F7.boolean.opBoolean","MERGE",FACE,{"derivedFrom":[makeQuery(id+"FbK9JrwXL36KEKy_1.4.F7.boolean.opBoolean","MERGE",FACE,{"derivedFrom":[makeQuery(id+"FbK9JrwXL36KEKy_1.3.F7.boolean.opBoolean","MERGE",FACE,{"derivedFrom":[makeQuery(id+"FbK9JrwXL36KEKy_1.2.F7.boolean.opBoolean","MERGE",FACE,{"derivedFrom":[makeQuery(id+"FbK9JrwXL36KEKy_1.1.F7.boolean.opBoolean","MERGE",FACE,{"derivedFrom":[makeQuery(id+"F7.boolean.opBoolean","MERGE",FACE,{"derivedFrom":[makeQuery(id+"F3.boolean.opBoolean","COPY",FACE,{"derivedFrom":makeQuery(id+"F3.opExtrude","CAP_FACE",FACE,{"disambiguationData":[OSD([sQuery(id+"F2.wireOp",EDGE,"E1"),sQuery(id+"F2.wireOp",EDGE,"E2")])],"isStart":false})}),makeQuery(id+"F7.opExtrude","CAP_FACE",FACE,{"disambiguationData":[OSD([subQ3,subQ2,subQ1,subQ0])],"isStart":false})]}),makeQuery(id+"FbK9JrwXL36KEKy_1.1.F7.opExtrude","CAP_FACE",FACE,{"disambiguationData":[OSD([subQ3,subQ2,subQ1,subQ0])],"isStart":false})]}),makeQuery(id+"FbK9JrwXL36KEKy_1.2.F7.opExtrude","CAP_FACE",FACE,{"disambiguationData":[OSD([subQ3,subQ2,subQ1,subQ0])],"isStart":false})]}),makeQuery(id+"FbK9JrwXL36KEKy_1.3.F7.opExtrude","CAP_FACE",FACE,{"disambiguationData":[OSD([subQ3,subQ2,subQ1,subQ0])],"isStart":false})]}),makeQuery(id+"FbK9JrwXL36KEKy_1.4.F7.opExtrude","CAP_FACE",FACE,{"disambiguationData":[OSD([subQ3,subQ2,subQ1,subQ0])],"isStart":false})]}),makeQuery(id+"FbK9JrwXL36KEKy_1.5.F7.opExtrude","CAP_FACE",FACE,{"disambiguationData":[OSD([subQ3,subQ2,subQ1,subQ0])],"isStart":false})]}),makeQuery(id+"FozZmEnTaBS6IKp_1.3.F17.opExtrude","SWEPT_FACE",FACE,{"disambiguationData":[OSD([sQuery(id+"F16.wireOp",EDGE,"E11")])]})]});}
            chamfer(context, id + "F18", {"entities" : qUnion([Q0, Q1, Q2, Q3, Q4, Q5]), "chamferType" : ChamferType.OFFSET_ANGLE, "width" : 11.13 * mm, "oppositeDirection" : false, "angle" : 65 * degree, "tangentPropagation" : true});
        }
        {
            var Q0;
            Q0=makeQuery(id+"FozZmEnTaBS6IKp_1.1.F17.boolean.opBoolean","INTERSECT",EDGE,{"derivedFrom":[makeQuery(id+"F1.opExtrude","CAP_FACE",FACE,{"disambiguationData":[OSD([sQuery(id+"F0.wireOp",EDGE,"E0")])],"isStart":false}),makeQuery(id+"FozZmEnTaBS6IKp_1.1.F17.opExtrude","SWEPT_FACE",FACE,{"disambiguationData":[OSD([sQuery(id+"F16.wireOp",EDGE,"E11")])]})]});
            var Q1;
            Q1=makeQuery(id+"FozZmEnTaBS6IKp_1.2.F17.boolean.opBoolean","INTERSECT",EDGE,{"derivedFrom":[makeQuery(id+"F1.opExtrude","CAP_FACE",FACE,{"disambiguationData":[OSD([sQuery(id+"F0.wireOp",EDGE,"E0")])],"isStart":false}),makeQuery(id+"FozZmEnTaBS6IKp_1.2.F17.opExtrude","SWEPT_FACE",FACE,{"disambiguationData":[OSD([sQuery(id+"F16.wireOp",EDGE,"E11")])]})]});
            var Q2;
            Q2=makeQuery(id+"FozZmEnTaBS6IKp_1.3.F17.boolean.opBoolean","INTERSECT",EDGE,{"derivedFrom":[makeQuery(id+"F1.opExtrude","CAP_FACE",FACE,{"disambiguationData":[OSD([sQuery(id+"F0.wireOp",EDGE,"E0")])],"isStart":false}),makeQuery(id+"FozZmEnTaBS6IKp_1.3.F17.opExtrude","SWEPT_FACE",FACE,{"disambiguationData":[OSD([sQuery(id+"F16.wireOp",EDGE,"E11")])]})]});
            var Q3;
            Q3=makeQuery(id+"FozZmEnTaBS6IKp_1.4.F17.boolean.opBoolean","INTERSECT",EDGE,{"derivedFrom":[makeQuery(id+"F1.opExtrude","CAP_FACE",FACE,{"disambiguationData":[OSD([sQuery(id+"F0.wireOp",EDGE,"E0")])],"isStart":false}),makeQuery(id+"FozZmEnTaBS6IKp_1.4.F17.opExtrude","SWEPT_FACE",FACE,{"disambiguationData":[OSD([sQuery(id+"F16.wireOp",EDGE,"E11")])]})]});
            var Q4;
            Q4=makeQuery(id+"FozZmEnTaBS6IKp_1.5.F17.boolean.opBoolean","INTERSECT",EDGE,{"derivedFrom":[makeQuery(id+"F1.opExtrude","CAP_FACE",FACE,{"disambiguationData":[OSD([sQuery(id+"F0.wireOp",EDGE,"E0")])],"isStart":false}),makeQuery(id+"FozZmEnTaBS6IKp_1.5.F17.opExtrude","SWEPT_FACE",FACE,{"disambiguationData":[OSD([sQuery(id+"F16.wireOp",EDGE,"E11")])]})]});
            var Q5;
            Q5=makeQuery(id+"F17.boolean.opBoolean","INTERSECT",EDGE,{"derivedFrom":[makeQuery(id+"F1.opExtrude","CAP_FACE",FACE,{"disambiguationData":[OSD([sQuery(id+"F0.wireOp",EDGE,"E0")])],"isStart":false}),makeQuery(id+"F17.opExtrude","SWEPT_FACE",FACE,{"disambiguationData":[OSD([sQuery(id+"F16.wireOp",EDGE,"E11")])]})]});
            chamfer(context, id + "F19", {"entities" : qUnion([Q0, Q1, Q2, Q3, Q4, Q5]), "chamferType" : ChamferType.OFFSET_ANGLE, "width" : 11.35 * mm, "oppositeDirection" : false, "angle" : 25 * degree, "tangentPropagation" : true});
        }
    });
